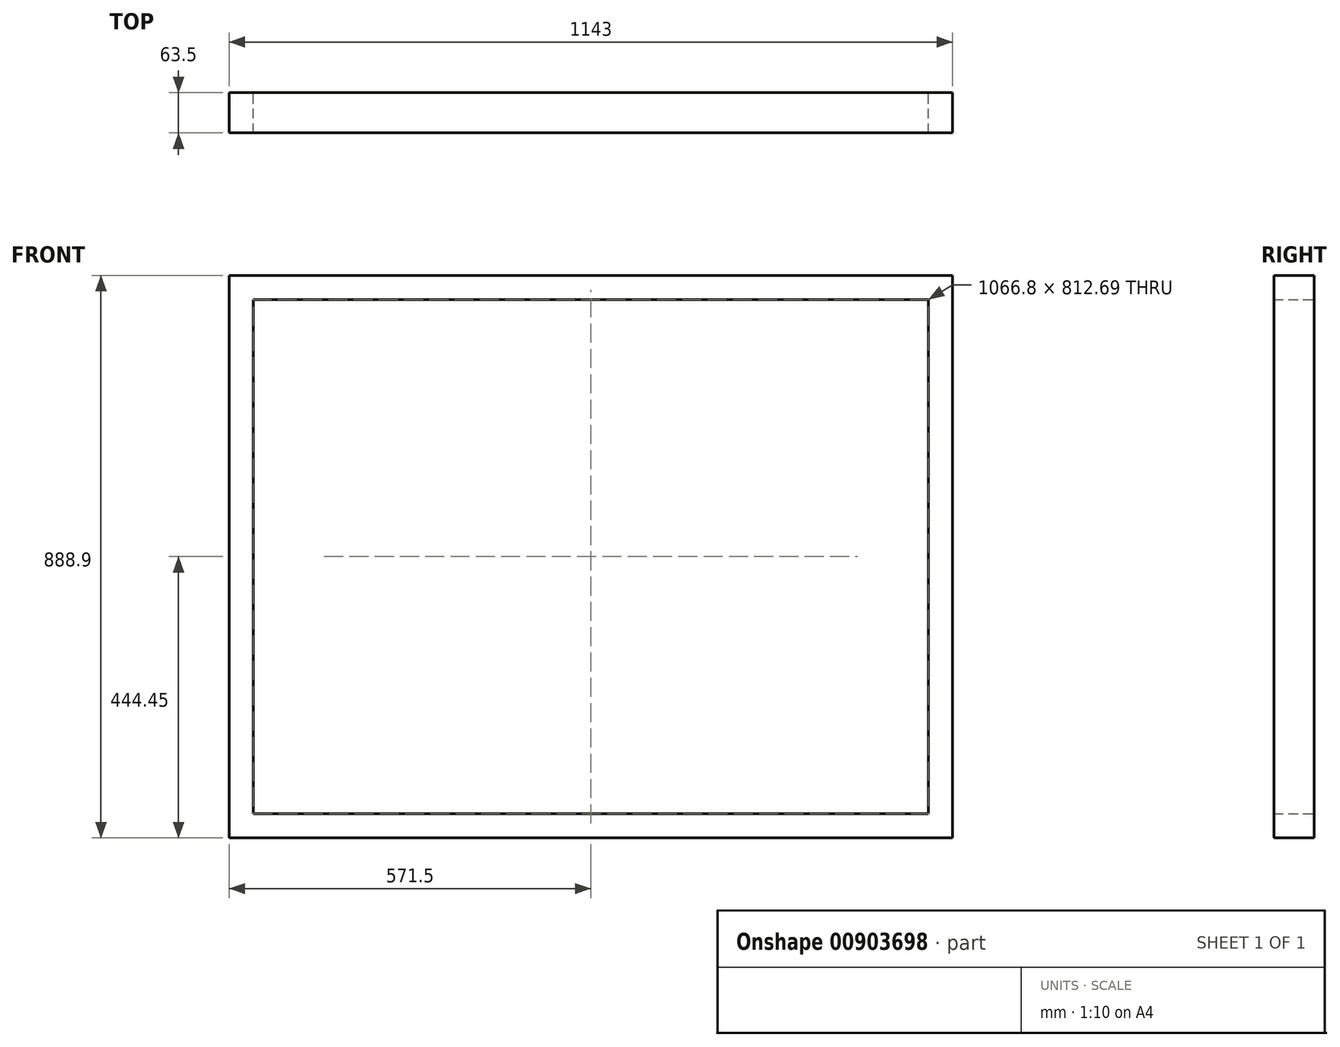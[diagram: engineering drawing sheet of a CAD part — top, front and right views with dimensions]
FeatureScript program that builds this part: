
annotation { "Feature Type Name" : "Feature", "Feature Type Description" : "" }
export const myFeature = defineFeature(function(context is Context, id is Id, definition is map)
    precondition{}
    {
        {
            var Q0;
            Q0=qCreatedBy(makeId("Front.planeOp"),FACE);
            var sketch = newSketch(context, id + "F0", { "sketchPlane" : qUnion([Q0])});
            skLineSegment(sketch, "E0.bottom", {"start": v(571.5, 444.45) * mm, "end": v(-571.5, 444.45) * mm});
            skLineSegment(sketch, "E0.top", {"start": v(571.5, -444.45) * mm, "end": v(-571.5, -444.45) * mm});
            skLineSegment(sketch, "E0.left", {"start": v(571.5, 444.45) * mm, "end": v(571.5, -444.45) * mm});
            skLineSegment(sketch, "E0.right", {"start": v(-571.5, 444.45) * mm, "end": v(-571.5, -444.45) * mm});
            skPoint(sketch, "E0.middle", {"position": v(0, 0) * mm});
            skLineSegment(sketch, "E1.bottom", {"start": v(533.4, 406.35) * mm, "end": v(-533.4, 406.35) * mm});
            skLineSegment(sketch, "E1.top", {"start": v(533.4, -406.35) * mm, "end": v(-533.4, -406.35) * mm});
            skLineSegment(sketch, "E1.left", {"start": v(533.4, 406.35) * mm, "end": v(533.4, -406.35) * mm});
            skLineSegment(sketch, "E1.right", {"start": v(-533.4, 406.35) * mm, "end": v(-533.4, -406.35) * mm});
            skSolve(sketch);
        }
        {
            var Q0;
            Q0=makeQuery(id+"F0.imprint","IMPRINT",FACE,{"disambiguationData":[TD([[makeQuery(id+"F0.imprint","IMPRINT",EDGE,{"derivedFrom":sQuery(id+"F0.wireOp",EDGE,"E0.bottom")}),1.0]])]});
            extrude(context, id + "F1", {"entities" : qUnion([Q0]), "depth" : 63.5 * mm, "offsetDistance" : 25.4 * mm});
        }
    });
